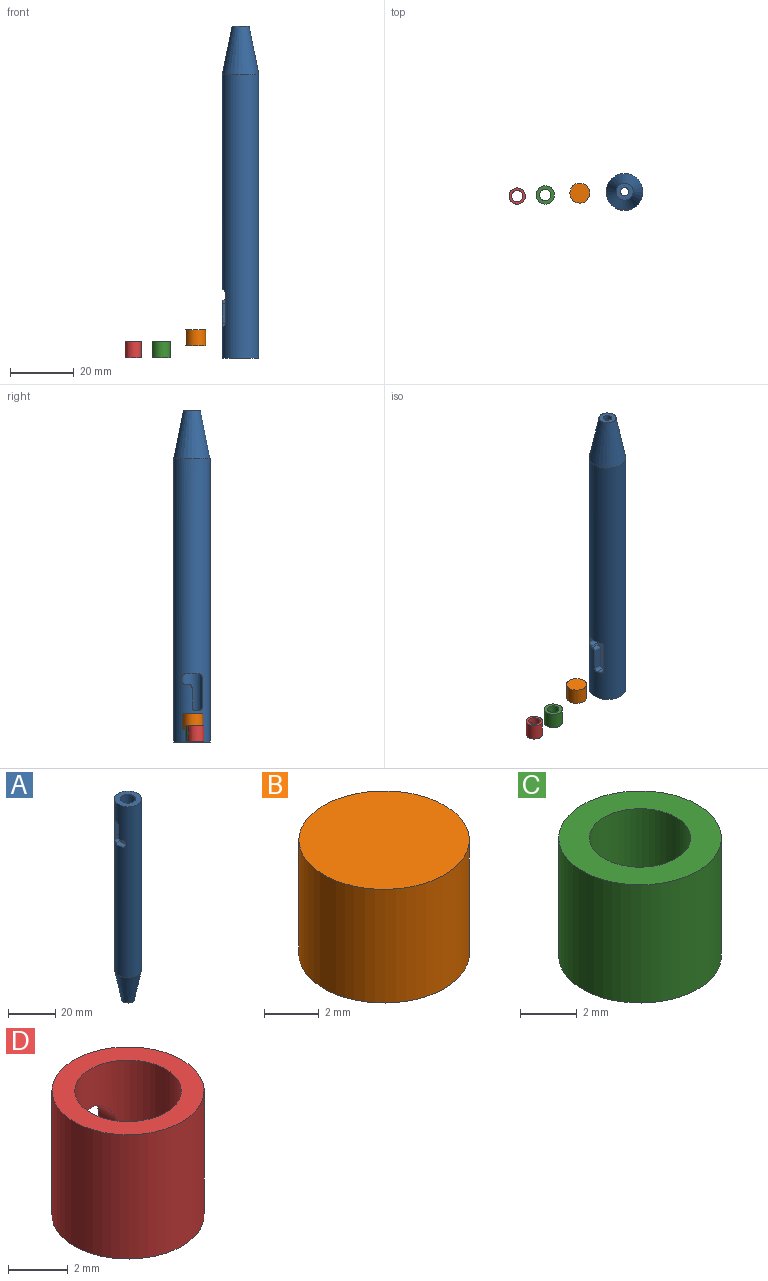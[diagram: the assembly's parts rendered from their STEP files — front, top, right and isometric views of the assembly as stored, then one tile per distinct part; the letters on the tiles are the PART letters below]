
ASSEMBLY  parts=4 mates=2
PART A: 22 faces, bbox 11.4x11.4x103.9 mm
  f0: cylinder r=1.78mm len=3.56mm, axis (0,0,-1), area 14.2mm2, adj f17,f20
  f1: cylinder r=3.17mm len=98.39mm, axis (0,0,-1), area 1893.3mm2, adj f3,f4,f5,f6,f7,f8,f10,f11
  f2: cylinder r=5.71mm len=88.61mm, axis (0,0,-1), area 3133.2mm2, adj f3,f4,f5,f6,f7,f8,f10,f11
  f3: plane 9.4x4.75mm, normal (0,-1,0), area 44.7mm2, adj f1,f2,f10,f15
  f4: plane 3.3x1.14mm, normal (0,0,-1), area 3.2mm2, adj f1,f2,f10,f11
  f5: plane 6.14x2.54mm, normal (0,1,0), area 15.6mm2, adj f1,f2,f11,f12
  f6: plane 3.21x0.99mm, normal (0,-0.08,-1), area 2.7mm2, adj f1,f2,f12,f13
  f7: plane 4.75x1.31mm, normal (0,1,0), area 6.2mm2, adj f1,f2,f13,f14
  f8: plane 4.32x3.39mm, normal (0,0,1), area 11.5mm2, adj f1,f2,f14,f15
  f9: plane 5.33x5.33mm, normal (0,0,-1), area 17.3mm2, adj f18,f19
  f10: cylinder r=1.02mm len=5.29mm, axis (-1,0,0), area 5.9mm2, adj f1,f2,f3,f4
  f11: cylinder r=1.02mm len=2.71mm, axis (-1,0,0), area 4.1mm2, adj f1,f2,f4,f5
  f12: cylinder r=1.02mm len=2.74mm, axis (-1,0,0), area 4.2mm2, adj f1,f2,f5,f6
  f13: cylinder r=1.02mm len=5.32mm, axis (-1,0,0), area 6.1mm2, adj f1,f2,f6,f7
  f14: cylinder r=1.02mm len=5.29mm, axis (1,0,0), area 5.9mm2, adj f1,f2,f7,f8
  f15: cylinder r=1.02mm len=5.29mm, axis (-1,0,0), area 5.9mm2, adj f1,f2,f3,f8
  f16: plane 11.43x11.43mm, normal (0,0,1), area 70.9mm2, adj f1,f2
  f17: plane 5.59x5.59mm, normal (0,0,1), area 14.6mm2, adj f0,f21
  f18: cone r=5.71mm half-angle=11.3deg, axis (0,0,1), area 409.3mm2, adj f2,f9
  f19: cylinder r=1.27mm len=3.3mm, axis (0,0,-1), area 26.3mm2, adj f9,f20
  f20: cone r=1.27mm half-angle=45deg, axis (0,0,1), area 6.9mm2, adj f0,f19
  f21: cone r=2.79mm half-angle=45deg, axis (0,0,1), area 10.1mm2, adj f1,f17
PART B: 3 faces, bbox 6.2x6.2x5.1 mm
  f0: cylinder r=3.11mm len=6.22mm, axis (0,0,-1), area 99.3mm2, adj f1,f2
  f1: plane 6.22x6.22mm, normal (0,0,1), area 30.4mm2, adj f0
  f2: plane 6.22x6.22mm, normal (0,0,-1), area 30.4mm2, adj f0
PART C: 4 faces, bbox 5.7x5.7x5.1 mm
  f0: cylinder r=1.78mm len=5.08mm, axis (0,0,-1), area 56.8mm2, adj f2,f3
  f1: cylinder r=2.86mm len=5.72mm, axis (0,0,-1), area 91.2mm2, adj f2,f3
  f2: plane 5.72x5.72mm, normal (0,0,1), area 15.7mm2, adj f0,f1
  f3: plane 5.72x5.72mm, normal (0,0,-1), area 15.7mm2, adj f0,f1
PART D: 5 faces, bbox 5.1x5.1x5.1 mm
  f0: cylinder r=1.78mm len=5.08mm, axis (0,0,-1), area 53.8mm2, adj f2,f3,f4
  f1: cylinder r=2.54mm len=5.08mm, axis (0,0,-1), area 78.2mm2, adj f2,f3,f4
  f2: plane 5.08x5.08mm, normal (0,0,1), area 10.3mm2, adj f0,f1
  f3: plane 5.08x5.08mm, normal (0,0,-1), area 10.3mm2, adj f0,f1
  f4: cylinder r=0.95mm len=1.91mm, axis (0,-1,0), area 4.8mm2, adj f0,f1
PLACE A rot(axis=(1,0,0),180deg) t=(1.77,2.23,49.41)mm
PLACE B t=(-12.22,1.94,0.17)mm
PLACE C t=(-23.05,1.39,-3.64)mm
PLACE D t=(-31.8,1.03,-3.64)mm
MATE planar A.f0 <-> D.f1  axis (0,0,-1) through (1.77,2.23,-3.64)mm
MATE planar A.f0 <-> C.f1  axis (0,0,-1) through (1.77,2.23,-3.64)mm
